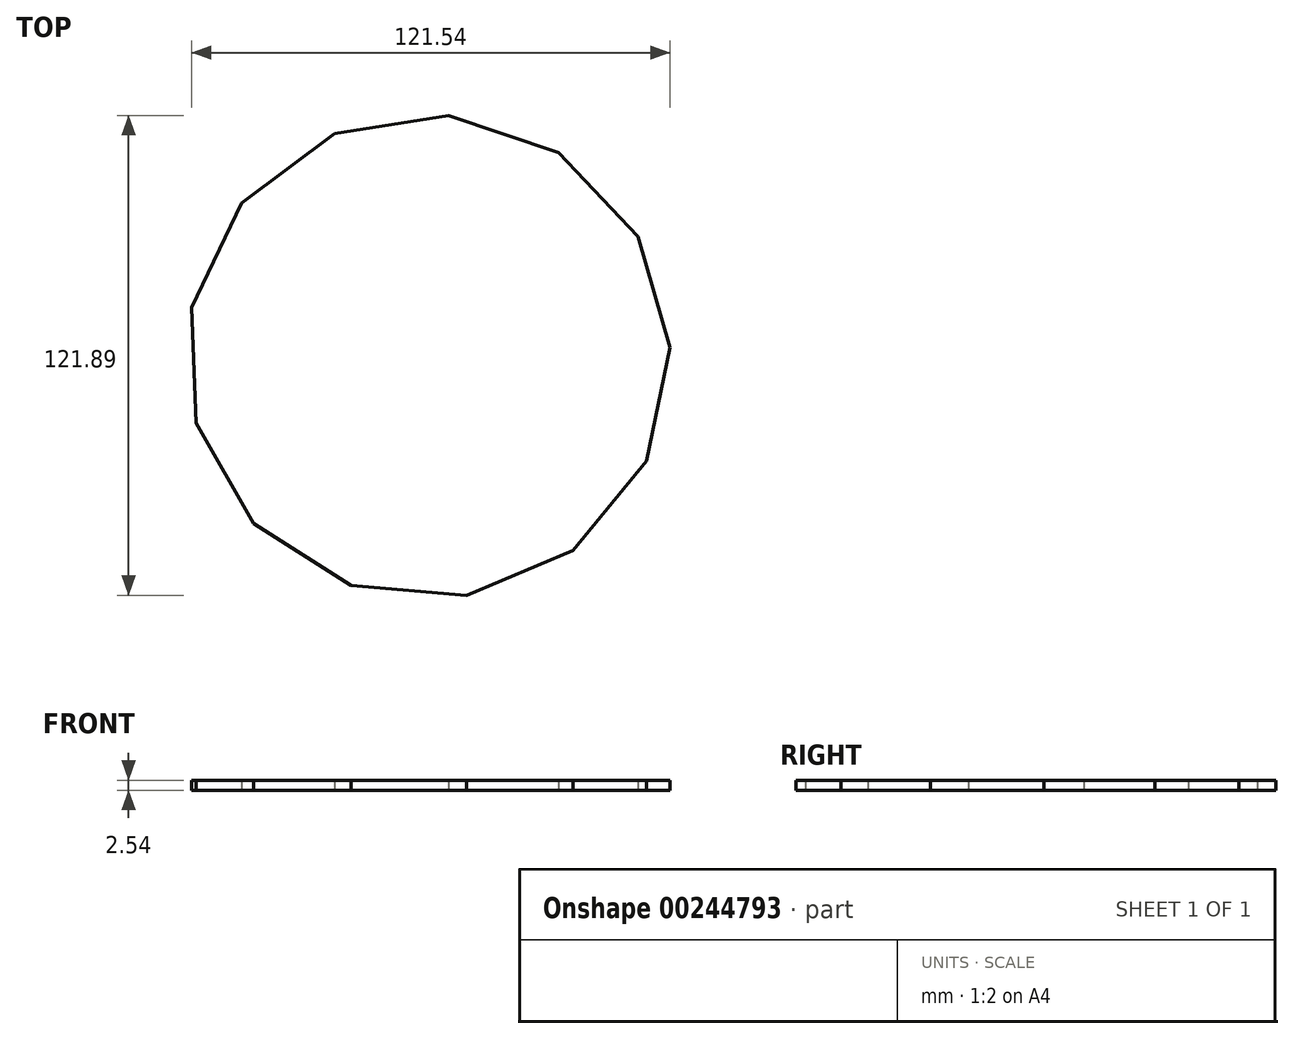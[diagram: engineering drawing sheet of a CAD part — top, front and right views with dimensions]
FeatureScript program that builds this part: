
annotation { "Feature Type Name" : "Feature", "Feature Type Description" : "" }
export const myFeature = defineFeature(function(context is Context, id is Id, definition is map)
    precondition{}
    {
        {
            var Q0;
            Q0=qCreatedBy(makeId("Top.planeOp"),FACE);
            var sketch = newSketch(context, id + "F0", { "sketchPlane" : qUnion([Q0])});
            skCircle(sketch, "E0.cCircle", {"center": v(0, 0) * mm, "radius": 59.65 * mm, "construction": true});
            skLineSegment(sketch, "E0.0", {"start": v(-44.45, -42.41) * mm, "end": v(-59.06, -16.9) * mm});
            skLineSegment(sketch, "E0.1", {"start": v(-59.06, -16.9) * mm, "end": v(-60.15, 12.49) * mm});
            skLineSegment(sketch, "E0.2", {"start": v(-60.15, 12.49) * mm, "end": v(-47.46, 39) * mm});
            skLineSegment(sketch, "E0.3", {"start": v(-47.46, 39) * mm, "end": v(-23.9, 56.6) * mm});
            skLineSegment(sketch, "E0.4", {"start": v(-23.9, 56.6) * mm, "end": v(5.14, 61.22) * mm});
            skLineSegment(sketch, "E0.5", {"start": v(5.14, 61.22) * mm, "end": v(33, 51.81) * mm});
            skLineSegment(sketch, "E0.6", {"start": v(33, 51.81) * mm, "end": v(53.3, 30.54) * mm});
            skLineSegment(sketch, "E0.7", {"start": v(53.3, 30.54) * mm, "end": v(61.4, 2.27) * mm});
            skLineSegment(sketch, "E0.8", {"start": v(61.4, 2.27) * mm, "end": v(55.42, -26.52) * mm});
            skLineSegment(sketch, "E0.9", {"start": v(55.42, -26.52) * mm, "end": v(36.74, -49.23) * mm});
            skLineSegment(sketch, "E0.10", {"start": v(36.74, -49.23) * mm, "end": v(9.66, -60.67) * mm});
            skLineSegment(sketch, "E0.11", {"start": v(9.66, -60.67) * mm, "end": v(-19.65, -58.2) * mm});
            skLineSegment(sketch, "E0.12", {"start": v(-19.65, -58.2) * mm, "end": v(-44.45, -42.41) * mm});
            skPoint(sketch, "E0.0.midPoint", {"position": v(-51.75, -29.65) * mm});
            skSolve(sketch);
        }
        {
            var Q0;
            Q0=makeQuery(id+"F0.imprint","IMPRINT",FACE,{"disambiguationData":[TD([[makeQuery(id+"F0.imprint","IMPRINT",EDGE,{"derivedFrom":sQuery(id+"F0.wireOp",EDGE,"E0.0")}),-1.0]])]});
            extrude(context, id + "F1", {"entities" : qUnion([Q0]), "depth" : 2.54 * mm});
        }
    });
